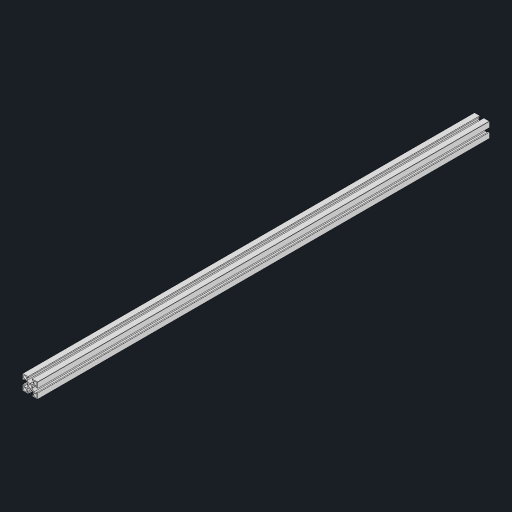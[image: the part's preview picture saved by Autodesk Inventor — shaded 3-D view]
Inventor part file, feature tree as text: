
AUTODESK INVENTOR PART (.ipt)
format: ipt  version: 2024.2 (Build 282272000, 272)  size: 230,400 bytes
history: native  units: mm
features: other x1, extrude x1, fillet x1, sketch x1
ambient origin geometry x8: Origin, YZ Plane, XZ Plane, XY Plane, X Axis, Y Axis, Z Axis, Center Point
bodies: Body1 (feature_tree)
feature tree (4):
  other  "솔리드1"
  extrude  "프로파일 길이 설정"  Depth=20.0mm
  fillet  "모서리"  Radius=20.0mm
  sketch  "스케치1"
